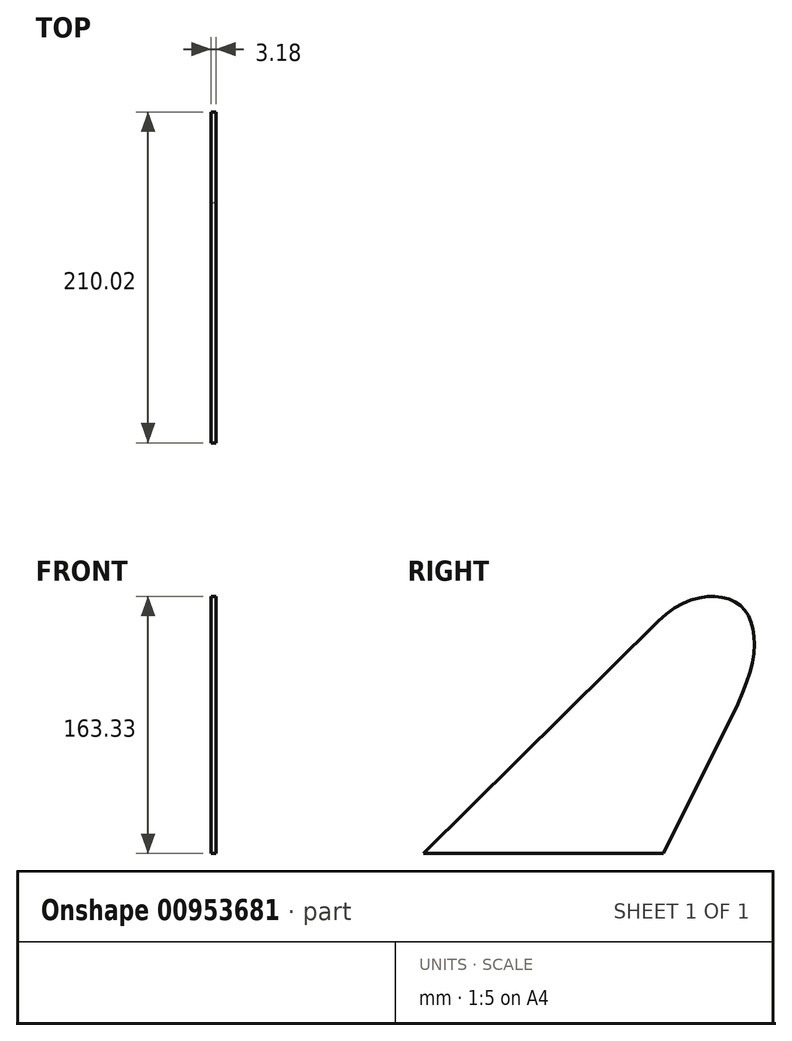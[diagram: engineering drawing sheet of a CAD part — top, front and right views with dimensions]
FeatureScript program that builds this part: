
annotation { "Feature Type Name" : "Feature", "Feature Type Description" : "" }
export const myFeature = defineFeature(function(context is Context, id is Id, definition is map)
    precondition{}
    {
        {
            var Q0;
            Q0=qCreatedBy(makeId("Right.planeOp"),FACE);
            var sketch = newSketch(context, id + "F0", { "sketchPlane" : qUnion([Q0])});
            skLineSegment(sketch, "E0", {"start": v(0, 0) * mm, "end": v(152.4, 0) * mm});
            skFitSpline(sketch, "E1", {"points": [v(199.4, 95.11) * mm, v(201.11, 157.33) * mm, v(149.19, 147.7) * mm], "startDerivative": vector(78.27, 158.4) * mm, "endDerivative": vector(-113, -111.86) * mm});
            skLineSegment(sketch, "E2", {"start": v(152.4, 0) * mm, "end": v(199.4, 95.11) * mm});
            skLineSegment(sketch, "E3", {"start": v(149.19, 147.7) * mm, "end": v(0, 0) * mm});
            skSolve(sketch);
        }
        {
            var Q0;
            Q0 = qSketchRegion(id + "F0", true);
            extrude(context, id + "F1", {"entities" : qUnion([Q0]), "depth" : 3.17 * mm, "offsetDistance" : 25.4 * mm});
        }
    });
